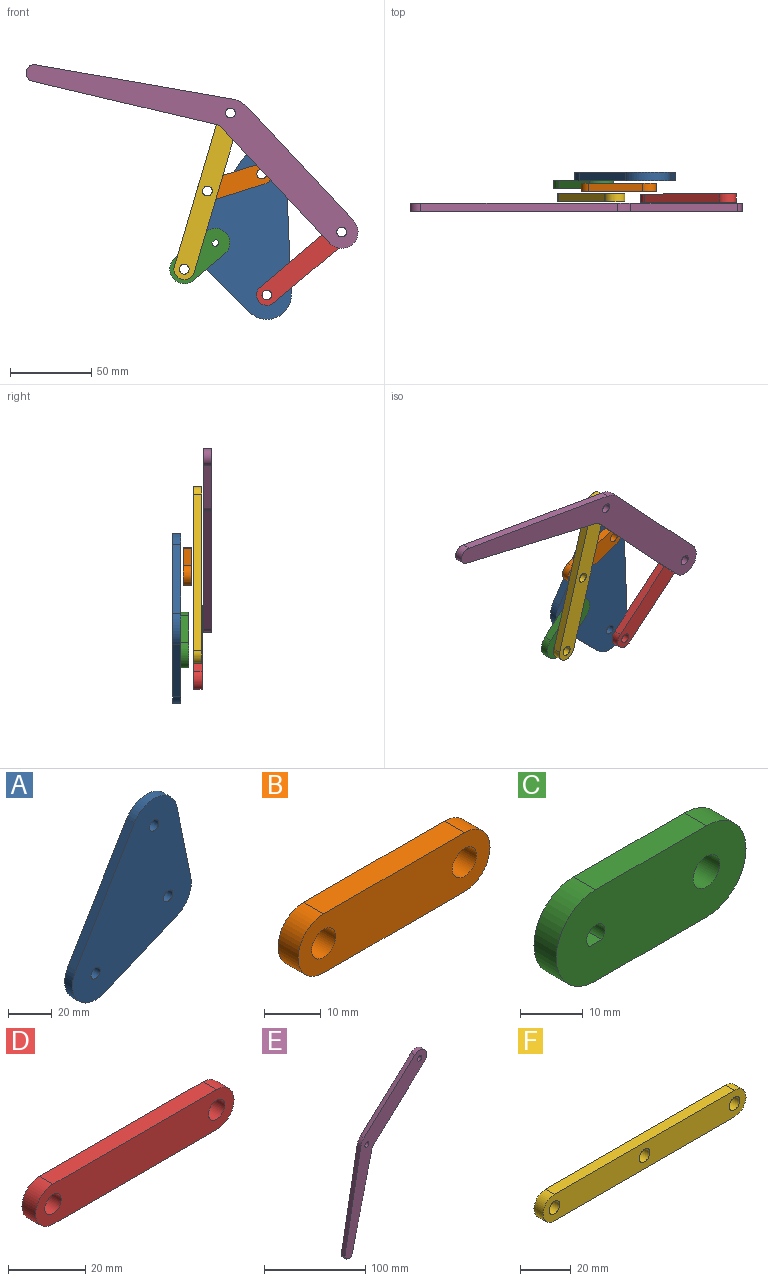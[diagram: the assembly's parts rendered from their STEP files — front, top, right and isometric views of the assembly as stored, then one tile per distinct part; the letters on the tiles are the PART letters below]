
ASSEMBLY  parts=6 mates=7
PART A: 11 faces, bbox 77x5x93.9 mm
  f0: plane 63.88x38mm, normal (-0.86,0,0.51), area 371.7mm2, adj f6,f7,f8,f10
  f1: plane 46.99x19.79mm, normal (0.39,0,-0.92), area 254.9mm2, adj f6,f7,f8,f9
  f2: cylinder r=3mm len=6mm, axis (0,1,0), area 94.2mm2, adj f6,f7
  f3: cylinder r=3mm len=6mm, axis (0,1,0), area 94.2mm2, adj f6,f7
  f4: plane 44.09x8.99mm, normal (0.98,0,0.2), area 225mm2, adj f6,f7,f9,f10
  f5: cylinder r=3mm len=6mm, axis (0,1,0), area 94.2mm2, adj f6,f7
  f6: plane 93.88x76.99mm, normal (0,-1,0), area 4301.8mm2, adj f0,f1,f2,f3,f4,f5,f8,f9
  f7: plane 93.88x76.99mm, normal (0,1,0), area 4301.8mm2, adj f0,f1,f2,f3,f4,f5,f8,f9
  f8: cylinder r=15mm len=22.67mm, axis (0,1,0), area 188mm2, adj f0,f1,f6,f7
  f9: cylinder r=15mm len=16.82mm, axis (0,1,0), area 103mm2, adj f1,f4,f6,f7
  f10: cylinder r=15mm len=27.59mm, axis (0,1,0), area 180.3mm2, adj f0,f4,f6,f7
PART B: 8 faces, bbox 47.7x5x12.7 mm
  f0: cylinder r=6.35mm len=12.7mm, axis (0,1,0), area 99.7mm2, adj f1,f5,f6,f7
  f1: plane 35x5mm, normal (0,0,1), area 175mm2, adj f0,f2,f6,f7
  f2: cylinder r=6.35mm len=12.7mm, axis (0,1,0), area 99.7mm2, adj f1,f5,f6,f7
  f3: cylinder r=3mm len=6mm, axis (0,1,0), area 94.2mm2, adj f6,f7
  f4: cylinder r=3mm len=6mm, axis (0,1,0), area 94.2mm2, adj f6,f7
  f5: plane 35x5mm, normal (0,0,-1), area 175mm2, adj f0,f2,f6,f7
  f6: plane 47.7x12.7mm, normal (0,-1,0), area 514.6mm2, adj f0,f1,f2,f3,f4,f5
  f7: plane 47.7x12.7mm, normal (0,1,0), area 514.6mm2, adj f0,f1,f2,f3,f4,f5
PART C: 9 faces, bbox 42.8x5x17.8 mm
  f0: plane 25x5mm, normal (0,0,-1), area 125mm2, adj f1,f4,f6,f7
  f1: cylinder r=8.91mm len=17.83mm, axis (0,1,0), area 140mm2, adj f0,f2,f6,f7
  f2: plane 25x5mm, normal (0,0,1), area 125mm2, adj f1,f4,f6,f7
  f3: cylinder r=2.05mm len=5mm, axis (0,1,0), area 49mm2, adj f6,f7,f8
  f4: cylinder r=8.91mm len=17.83mm, axis (0,1,0), area 140mm2, adj f0,f2,f6,f7
  f5: cylinder r=3mm len=6mm, axis (0,1,0), area 94.2mm2, adj f6,f7
  f6: plane 42.83x17.83mm, normal (0,-1,0), area 655mm2, adj f0,f1,f2,f3,f4,f5,f8
  f7: plane 42.83x17.83mm, normal (0,1,0), area 655mm2, adj f0,f1,f2,f3,f4,f5,f8
  f8: plane 5x2.79mm, normal (0,0,1), area 14mm2, adj f3,f6,f7
PART D: 8 faces, bbox 72.7x5x12.7 mm
  f0: cylinder r=6.35mm len=12.7mm, axis (0,1,0), area 99.7mm2, adj f1,f5,f6,f7
  f1: plane 60x5mm, normal (0,0,1), area 300mm2, adj f0,f2,f6,f7
  f2: cylinder r=6.35mm len=12.7mm, axis (0,1,0), area 99.8mm2, adj f1,f5,f6,f7
  f3: cylinder r=3mm len=6mm, axis (0,1,0), area 94.2mm2, adj f6,f7
  f4: cylinder r=3mm len=6mm, axis (0,1,0), area 94.2mm2, adj f6,f7
  f5: plane 60x5mm, normal (0,0,-1), area 300mm2, adj f0,f2,f6,f7
  f6: plane 72.7x12.7mm, normal (0,-1,0), area 832.1mm2, adj f0,f1,f2,f3,f4,f5
  f7: plane 72.7x12.7mm, normal (0,1,0), area 832.1mm2, adj f0,f1,f2,f3,f4,f5
PART E: 12 faces, bbox 114.2x5x203.1 mm
  f0: plane 113.23x27.54mm, normal (0.97,0,-0.24), area 582.6mm2, adj f5,f6,f7,f11
  f1: plane 72.46x66.7mm, normal (0.68,0,-0.74), area 492.4mm2, adj f2,f6,f7,f11
  f2: cylinder r=10.03mm len=16.82mm, axis (0,1,0), area 152.4mm2, adj f1,f3,f6,f7
  f3: plane 70.62x65mm, normal (-0.68,0,0.74), area 479.9mm2, adj f2,f6,f7,f10
  f4: plane 120.35x21.97mm, normal (-0.98,0,0.18), area 611.7mm2, adj f5,f6,f7,f10
  f5: cylinder r=5.19mm len=10.23mm, axis (0,1,0), area 83.1mm2, adj f0,f4,f6,f7
  f6: plane 203.07x114.23mm, normal (0,-1,0), area 3848.6mm2, adj f0,f1,f2,f3,f4,f5,f8,f9
  f7: plane 203.07x114.23mm, normal (0,1,0), area 3848.6mm2, adj f0,f1,f2,f3,f4,f5,f8,f9
  f8: cylinder r=3mm len=6mm, axis (0,-1,0), area 94.2mm2, adj f6,f7
  f9: cylinder r=3mm len=6mm, axis (0,-1,0), area 94.2mm2, adj f6,f7
  f10: cylinder r=15mm len=8.34mm, axis (0,-1,0), area 48.5mm2, adj f3,f4,f6,f7
  f11: cylinder r=5mm len=5mm, axis (0,1,0), area 14.7mm2, adj f0,f1,f6,f7
PART F: 9 faces, bbox 112.7x5x12.7 mm
  f0: cylinder r=6.35mm len=12.7mm, axis (0,1,0), area 99.8mm2, adj f1,f6,f7,f8
  f1: plane 100x5mm, normal (0,0,1), area 500mm2, adj f0,f2,f7,f8
  f2: cylinder r=6.35mm len=12.7mm, axis (0,1,0), area 99.7mm2, adj f1,f6,f7,f8
  f3: cylinder r=3mm len=6mm, axis (0,1,0), area 94.2mm2, adj f7,f8
  f4: cylinder r=3mm len=6mm, axis (0,1,0), area 94.2mm2, adj f7,f8
  f5: cylinder r=3mm len=6mm, axis (0,1,0), area 94.2mm2, adj f7,f8
  f6: plane 100x5mm, normal (0,0,-1), area 500mm2, adj f0,f2,f7,f8
  f7: plane 112.7x12.7mm, normal (0,-1,0), area 1311.9mm2, adj f0,f1,f2,f3,f4,f5,f6
  f8: plane 112.7x12.7mm, normal (0,1,0), area 1311.9mm2, adj f0,f1,f2,f3,f4,f5,f6
PLACE A rot(axis=(0,1,0),146.8deg) t=(105.18,36.37,72.65)mm fixed
PLACE B rot(axis=(0.15,0,-0.99),180deg) t=(72.15,24.77,20.65)mm
PLACE C rot(axis=(0,1,0),139.7deg) t=(50.8,31.37,-24.46)mm
PLACE D rot(axis=(0,-1,0),40.1deg) t=(114.93,23.27,-29.06)mm
PLACE E rot(axis=(0,1,0),89.6deg) t=(-46.74,17.47,-368.66)mm
PLACE F rot(axis=(0,1,0),106.5deg) t=(55.46,23.37,15.4)mm
MATE revolute D.f0 <-> E.f2  axis (0,-1,0) through (137.89,18.27,-9.75)mm
MATE revolute A.f2 <-> B.f2  axis (0,-1,0) through (88.85,31.37,25.9)mm
MATE revolute B.f0 <-> F.f4  axis (0,-1,0) through (55.46,24.77,15.4)mm
MATE revolute C.f5 <-> F.f0  axis (0,-1,0) through (41.27,26.37,-32.55)mm
MATE revolute F.f2 <-> E.f8  axis (0,1,0) through (69.64,18.37,63.34)mm
MATE revolute A.f5 <-> D.f2  axis (0,-1,0) through (91.97,31.37,-48.37)mm
MATE revolute C.f3 <-> A.f3  axis (0,1,0) through (60.33,31.37,-16.37)mm
